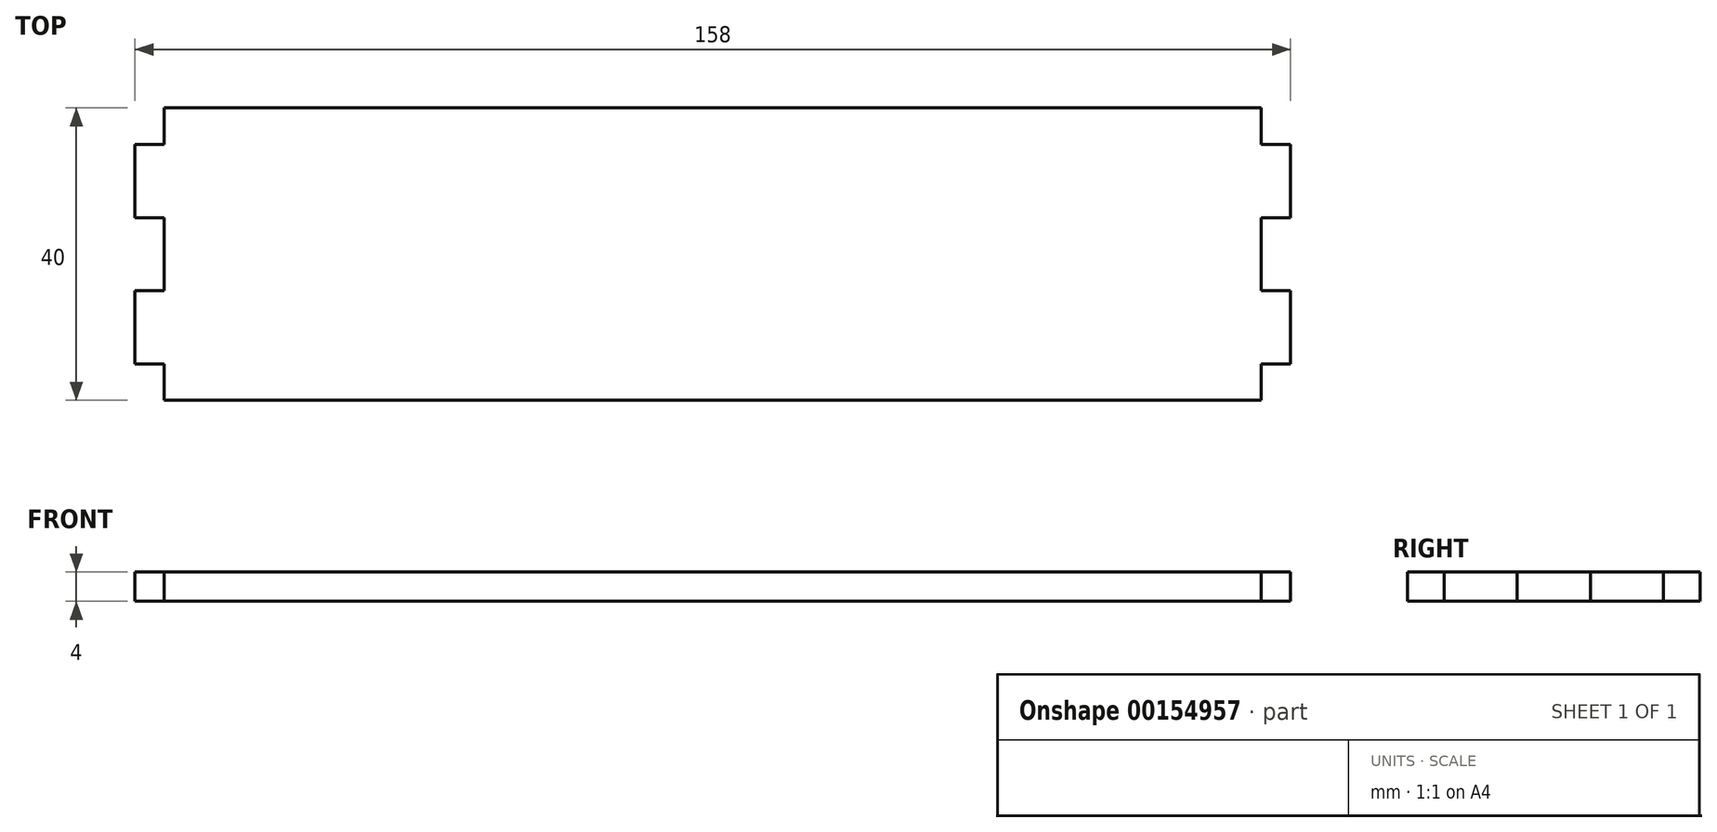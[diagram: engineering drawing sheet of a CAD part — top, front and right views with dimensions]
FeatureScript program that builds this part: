
annotation { "Feature Type Name" : "Feature", "Feature Type Description" : "" }
export const myFeature = defineFeature(function(context is Context, id is Id, definition is map)
    precondition{}
    {
        {
            var Q0;
            Q0=qCreatedBy(makeId("Top.planeOp"),FACE);
            var sketch = newSketch(context, id + "F0", { "sketchPlane" : qUnion([Q0])});
            skLineSegment(sketch, "E0.bottom", {"start": v(75, 18.82) * mm, "end": v(-75, 18.82) * mm});
            skLineSegment(sketch, "E0.top", {"start": v(75, -21.18) * mm, "end": v(-75, -21.18) * mm});
            skLineSegment(sketch, "E0.left", {"start": v(75, 18.82) * mm, "end": v(75, -21.18) * mm});
            skLineSegment(sketch, "E0.right", {"start": v(-75, 18.82) * mm, "end": v(-75, -21.18) * mm});
            skPoint(sketch, "E0.middle", {"position": v(0, -1.18) * mm});
            skSolve(sketch);
        }
        {
            var Q0;
            Q0 = qSketchRegion(id + "F0", true);
            extrude(context, id + "F1", {"entities" : qUnion([Q0]), "depth" : 4 * mm});
        }
        {
            var Q0;
            Q0=makeQuery(id+"F1.opExtrude","CAP_FACE",FACE,{"disambiguationData":[OSD([sQuery(id+"F0.wireOp",EDGE,"E0.bottom"),sQuery(id+"F0.wireOp",EDGE,"E0.top"),sQuery(id+"F0.wireOp",EDGE,"E0.left"),sQuery(id+"F0.wireOp",EDGE,"E0.right")])],"isStart":false});
            var sketch = newSketch(context, id + "F2", { "sketchPlane" : qUnion([Q0])});
            skLineSegment(sketch, "E1", {"start": v(-75, 18.82) * mm, "end": v(-75, 13.82) * mm});
            skLineSegment(sketch, "E2", {"start": v(-75, 13.82) * mm, "end": v(-79, 13.82) * mm});
            skLineSegment(sketch, "E3", {"start": v(-79, 13.82) * mm, "end": v(-79, 3.82) * mm});
            skLineSegment(sketch, "E4", {"start": v(-79, 3.82) * mm, "end": v(-75, 3.82) * mm});
            skLineSegment(sketch, "E5", {"start": v(-75, 3.82) * mm, "end": v(-75, 13.82) * mm});
            skLineSegment(sketch, "E6.0.1.0", {"start": v(-75, -6.18) * mm, "end": v(-79, -6.18) * mm});
            skLineSegment(sketch, "E6.0.1.1", {"start": v(-79, -6.18) * mm, "end": v(-79, -16.18) * mm});
            skLineSegment(sketch, "E6.0.1.2", {"start": v(-75, -16.18) * mm, "end": v(-75, -6.18) * mm});
            skLineSegment(sketch, "E6.0.1.3", {"start": v(-79, -16.18) * mm, "end": v(-75, -16.18) * mm});
            skLineSegment(sketch, "E6.direction1", {"start": v(-79, 13.82) * mm, "end": v(-54, 13.82) * mm, "construction": true});
            skLineSegment(sketch, "E6.direction2", {"start": v(-79, 13.82) * mm, "end": v(-79, -6.18) * mm, "construction": true});
            skLineSegment(sketch, "E7", {"start": v(0, 18.82) * mm, "end": v(0, 13.61) * mm});
            skPoint(sketch, "E7.endSnap0", {"position": v(0, 18.82) * mm});
            skLineSegment(sketch, "E8.MirrorCS", {"start": v(79, 13.82) * mm, "end": v(79, 3.82) * mm});
            skLineSegment(sketch, "E9.MirrorCS", {"start": v(79, -6.18) * mm, "end": v(79, -16.18) * mm});
            skLineSegment(sketch, "E10.MirrorCS", {"start": v(75, -6.18) * mm, "end": v(79, -6.18) * mm});
            skLineSegment(sketch, "E11.MirrorCS", {"start": v(75, -16.18) * mm, "end": v(75, -6.18) * mm});
            skLineSegment(sketch, "E12.MirrorCS", {"start": v(79, -16.18) * mm, "end": v(75, -16.18) * mm});
            skLineSegment(sketch, "E13.MirrorCS", {"start": v(79, 13.82) * mm, "end": v(79, -6.18) * mm, "construction": true});
            skLineSegment(sketch, "E14.MirrorCS", {"start": v(75, 13.82) * mm, "end": v(79, 13.82) * mm});
            skLineSegment(sketch, "E15.MirrorCS", {"start": v(79, 3.82) * mm, "end": v(75, 3.82) * mm});
            skLineSegment(sketch, "E16.MirrorCS", {"start": v(75, 3.82) * mm, "end": v(75, 13.82) * mm});
            skLineSegment(sketch, "E17.MirrorCS", {"start": v(75, 18.82) * mm, "end": v(75, 13.82) * mm});
            skSolve(sketch);
        }
        {
            var Q0;
            Q0 = qSketchRegion(id + "F2", true);
            extrude(context, id + "F3", {"entities" : qUnion([Q0]), "operationType" : NewBodyOperationType.ADD, "oppositeDirection" : true, "depth" : 4 * mm});
        }
    });
